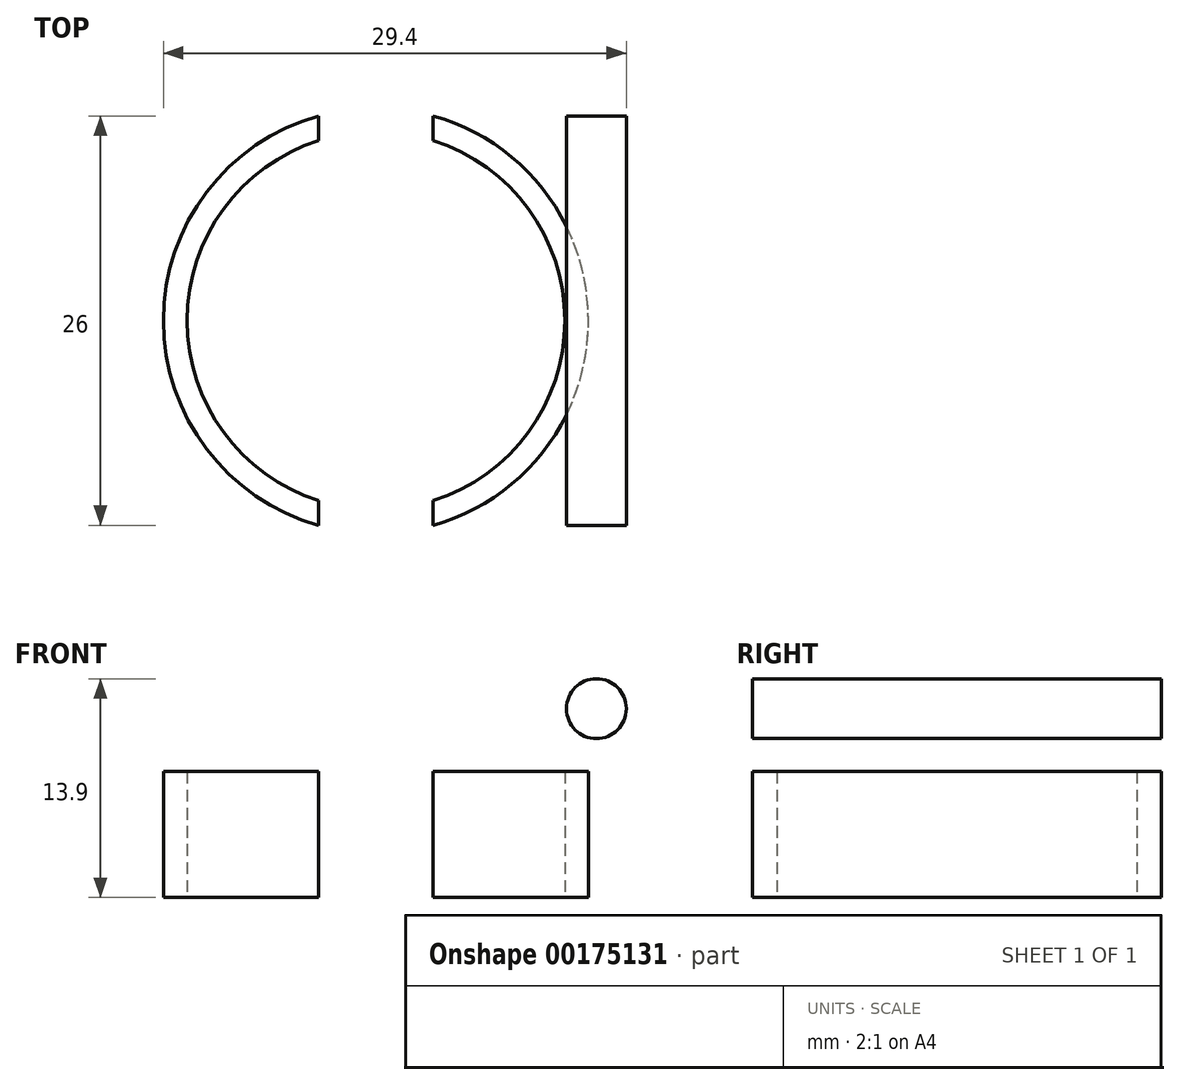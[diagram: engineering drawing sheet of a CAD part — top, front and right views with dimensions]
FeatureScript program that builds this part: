
annotation { "Feature Type Name" : "Feature", "Feature Type Description" : "" }
export const myFeature = defineFeature(function(context is Context, id is Id, definition is map)
    precondition{}
    {
        {
            var Q0;
            Q0=qCreatedBy(makeId("Top.planeOp"),FACE);
            var sketch = newSketch(context, id + "F0", { "sketchPlane" : qUnion([Q0])});
            skCircle(sketch, "E0", {"center": v(0, 0) * mm, "radius": 12 * mm});
            skCircle(sketch, "E1", {"center": v(0, 0) * mm, "radius": 10.25 * mm});
            skCircle(sketch, "E2", {"center": v(0, 0) * mm, "radius": 4.25 * mm});
            skCircle(sketch, "E3", {"center": v(0, 0) * mm, "radius": 2.6 * mm});
            skCircle(sketch, "E4", {"center": v(0, -7) * mm, "radius": 2.6 * mm});
            skCircle(sketch, "E5", {"center": v(0, 0) * mm, "radius": 7 * mm, "construction": true});
            skCircle(sketch, "E6", {"center": v(-7, 0) * mm, "radius": 1.6 * mm});
            skCircle(sketch, "E7", {"center": v(7, 0) * mm, "radius": 1.6 * mm});
            skCircle(sketch, "E8", {"center": v(0, 7) * mm, "radius": 1.6 * mm});
            skCircle(sketch, "E9", {"center": v(4.95, 4.95) * mm, "radius": 1.6 * mm});
            skCircle(sketch, "E10.MirrorC", {"center": v(-4.95, 4.95) * mm, "radius": 1.6 * mm});
            skCircle(sketch, "E11", {"center": v(0, 0) * mm, "radius": 13.5 * mm});
            skLineSegment(sketch, "E12", {"start": v(-3.38, 13.07) * mm, "end": v(-2.98, 11.62) * mm});
            skLineSegment(sketch, "E13", {"start": v(-13, 3.65) * mm, "end": v(-11.53, 3.32) * mm});
            skLineSegment(sketch, "E14.MirrorCS", {"start": v(3.38, 13.07) * mm, "end": v(2.98, 11.62) * mm});
            skLineSegment(sketch, "E15.MirrorCS", {"start": v(13, 3.65) * mm, "end": v(11.53, 3.32) * mm});
            skLineSegment(sketch, "E16.MirrorCS", {"start": v(-13, -3.65) * mm, "end": v(-11.53, -3.32) * mm});
            skLineSegment(sketch, "E17.MirrorCS", {"start": v(-3.38, -13.07) * mm, "end": v(-2.98, -11.62) * mm});
            skLineSegment(sketch, "E18.MirrorCS", {"start": v(3.38, -13.07) * mm, "end": v(2.98, -11.62) * mm});
            skLineSegment(sketch, "E19.MirrorCS", {"start": v(13, -3.65) * mm, "end": v(11.53, -3.32) * mm});
            skLineSegment(sketch, "E20.bottom", {"start": v(16.5, 13) * mm, "end": v(-16.5, 13) * mm});
            skLineSegment(sketch, "E20.top", {"start": v(16.5, -13) * mm, "end": v(-16.5, -13) * mm});
            skLineSegment(sketch, "E20.left", {"start": v(16.5, 13) * mm, "end": v(16.5, -13) * mm});
            skLineSegment(sketch, "E20.right", {"start": v(-16.5, 13) * mm, "end": v(-16.5, -13) * mm});
            skSolve(sketch);
        }
        {
            var Q0;
            Q0=makeQuery(id+"F0.imprint","IMPRINT",FACE,{"disambiguationData":[TD([[makeQuery(id+"F0.imprint","IMPRINT",EDGE,{"derivedFrom":sQuery(id+"F0.wireOp",EDGE,"E2")}),1.0]])]});
            extrude(context, id + "F1", {"entities" : qUnion([Q0]), "depth" : 8 * mm});
        }
        {
            var Q0;
            Q0=makeQuery(id+"F0.imprint","IMPRINT",FACE,{"disambiguationData":[TD([[makeQuery(id+"F0.imprint","IMPRINT",EDGE,{"derivedFrom":sQuery(id+"F0.wireOp",EDGE,"E1")}),1.0]])]});
            extrude(context, id + "F2", {"entities" : qUnion([Q0]), "operationType" : NewBodyOperationType.ADD, "depth" : 8 * mm});
        }
        {
            var Q0;
            Q0=makeQuery(id+"F0.imprint","IMPRINT",FACE,{"disambiguationData":[TD([[makeQuery(id+"F0.imprint","IMPRINT",EDGE,{"derivedFrom":sQuery(id+"F0.wireOp",EDGE,"E0")}),1.0]])]});
            var Q1;
            {var subQ0=sQuery(id+"F0.wireOp",EDGE,"E15.MirrorCS");Q1=makeQuery(id+"F0.imprint","IMPRINT",FACE,{"disambiguationData":[TD([[makeQuery(id+"F0.imprint","IMPRINT",EDGE,{"derivedFrom":subQ0}),-1.0]])]});}
            var Q2;
            {var subQ0=sQuery(id+"F0.wireOp",EDGE,"E12");var subQ1=sQuery(id+"F0.wireOp",EDGE,"E0");var subQ2=makeQuery(id+"F0.imprint","INTERSECT",VERTEX,{"derivedFrom":[subQ1,subQ0]});Q2=makeQuery(id+"F0.imprint","IMPRINT",FACE,{"disambiguationData":[TD([[makeQuery(id+"F0.imprint","IMPRINT",EDGE,{"disambiguationData":[TD([[subQ2,1.0]])],"derivedFrom":subQ1}),-1.0]])]});}
            var Q3;
            {var subQ0=sQuery(id+"F0.wireOp",EDGE,"E20.left");Q3=makeQuery(id+"F0.imprint","IMPRINT",FACE,{"disambiguationData":[TD([[makeQuery(id+"F0.imprint","IMPRINT",EDGE,{"derivedFrom":subQ0}),-1.0]])]});}
            var Q4;
            {var subQ0=sQuery(id+"F0.wireOp",EDGE,"E15.MirrorCS");Q4=makeQuery(id+"F0.imprint","IMPRINT",FACE,{"disambiguationData":[TD([[makeQuery(id+"F0.imprint","IMPRINT",EDGE,{"derivedFrom":subQ0}),1.0]])]});}
            var Q5;
            {var subQ0=sQuery(id+"F0.wireOp",EDGE,"E19.MirrorCS");Q5=makeQuery(id+"F0.imprint","IMPRINT",FACE,{"disambiguationData":[TD([[makeQuery(id+"F0.imprint","IMPRINT",EDGE,{"derivedFrom":subQ0}),1.0]])]});}
            var Q6;
            {var subQ0=sQuery(id+"F0.wireOp",EDGE,"E17.MirrorCS");var subQ1=sQuery(id+"F0.wireOp",EDGE,"E0");var subQ2=makeQuery(id+"F0.imprint","INTERSECT",VERTEX,{"derivedFrom":[subQ1,subQ0]});Q6=makeQuery(id+"F0.imprint","IMPRINT",FACE,{"disambiguationData":[TD([[makeQuery(id+"F0.imprint","IMPRINT",EDGE,{"disambiguationData":[TD([[subQ2,-1.0]])],"derivedFrom":subQ1}),-1.0]])]});}
            var Q7;
            {var subQ0=sQuery(id+"F0.wireOp",EDGE,"E16.MirrorCS");Q7=makeQuery(id+"F0.imprint","IMPRINT",FACE,{"disambiguationData":[TD([[makeQuery(id+"F0.imprint","IMPRINT",EDGE,{"derivedFrom":subQ0}),-1.0]])]});}
            var Q8;
            {var subQ0=sQuery(id+"F0.wireOp",EDGE,"E20.right");Q8=makeQuery(id+"F0.imprint","IMPRINT",FACE,{"disambiguationData":[TD([[makeQuery(id+"F0.imprint","IMPRINT",EDGE,{"derivedFrom":subQ0}),1.0]])]});}
            var Q9;
            {var subQ0=sQuery(id+"F0.wireOp",EDGE,"E13");Q9=makeQuery(id+"F0.imprint","IMPRINT",FACE,{"disambiguationData":[TD([[makeQuery(id+"F0.imprint","IMPRINT",EDGE,{"derivedFrom":subQ0}),-1.0]])]});}
            var Q10;
            {var subQ0=sQuery(id+"F0.wireOp",EDGE,"E13");Q10=makeQuery(id+"F0.imprint","IMPRINT",FACE,{"disambiguationData":[TD([[makeQuery(id+"F0.imprint","IMPRINT",EDGE,{"derivedFrom":subQ0}),1.0]])]});}
            extrude(context, id + "F3", {"entities" : qUnion([Q0, Q1, Q2, Q3, Q4, Q5, Q6, Q7, Q8, Q9, Q10]), "operationType" : NewBodyOperationType.ADD, "depth" : 8 * mm});
        }
        {
            var Q0;
            {var subQ0=sQuery(id+"F0.wireOp",EDGE,"E16.MirrorCS");Q0=makeQuery(id+"F0.imprint","IMPRINT",FACE,{"disambiguationData":[TD([[makeQuery(id+"F0.imprint","IMPRINT",EDGE,{"derivedFrom":subQ0}),-1.0]])]});}
            var Q1;
            {var subQ0=sQuery(id+"F0.wireOp",EDGE,"E19.MirrorCS");Q1=makeQuery(id+"F0.imprint","IMPRINT",FACE,{"disambiguationData":[TD([[makeQuery(id+"F0.imprint","IMPRINT",EDGE,{"derivedFrom":subQ0}),1.0]])]});}
            var Q2;
            {var subQ0=sQuery(id+"F0.wireOp",EDGE,"E15.MirrorCS");Q2=makeQuery(id+"F0.imprint","IMPRINT",FACE,{"disambiguationData":[TD([[makeQuery(id+"F0.imprint","IMPRINT",EDGE,{"derivedFrom":subQ0}),-1.0]])]});}
            var Q3;
            {var subQ0=sQuery(id+"F0.wireOp",EDGE,"E13");Q3=makeQuery(id+"F0.imprint","IMPRINT",FACE,{"disambiguationData":[TD([[makeQuery(id+"F0.imprint","IMPRINT",EDGE,{"derivedFrom":subQ0}),1.0]])]});}
            var Q4;
            {var subQ0=sQuery(id+"F0.wireOp",EDGE,"E17.MirrorCS");var subQ1=sQuery(id+"F0.wireOp",EDGE,"E0");var subQ2=makeQuery(id+"F0.imprint","INTERSECT",VERTEX,{"derivedFrom":[subQ1,subQ0]});Q4=makeQuery(id+"F0.imprint","IMPRINT",FACE,{"disambiguationData":[TD([[makeQuery(id+"F0.imprint","IMPRINT",EDGE,{"disambiguationData":[TD([[subQ2,-1.0]])],"derivedFrom":subQ1}),-1.0]])]});}
            var Q5;
            {var subQ0=sQuery(id+"F0.wireOp",EDGE,"E13");Q5=makeQuery(id+"F0.imprint","IMPRINT",FACE,{"disambiguationData":[TD([[makeQuery(id+"F0.imprint","IMPRINT",EDGE,{"derivedFrom":subQ0}),-1.0]])]});}
            var Q6;
            {var subQ0=sQuery(id+"F0.wireOp",EDGE,"E15.MirrorCS");Q6=makeQuery(id+"F0.imprint","IMPRINT",FACE,{"disambiguationData":[TD([[makeQuery(id+"F0.imprint","IMPRINT",EDGE,{"derivedFrom":subQ0}),1.0]])]});}
            var Q7;
            {var subQ0=sQuery(id+"F0.wireOp",EDGE,"E12");var subQ1=sQuery(id+"F0.wireOp",EDGE,"E0");var subQ2=makeQuery(id+"F0.imprint","INTERSECT",VERTEX,{"derivedFrom":[subQ1,subQ0]});Q7=makeQuery(id+"F0.imprint","IMPRINT",FACE,{"disambiguationData":[TD([[makeQuery(id+"F0.imprint","IMPRINT",EDGE,{"disambiguationData":[TD([[subQ2,1.0]])],"derivedFrom":subQ1}),-1.0]])]});}
            extrude(context, id + "F4", {"entities" : qUnion([Q0, Q1, Q2, Q3, Q4, Q5, Q6, Q7]), "operationType" : NewBodyOperationType.ADD, "endBound" : BoundingType.SYMMETRIC, "depth" : 16 * mm});
        }
        {
            var Q0;
            {var subQ0=sQuery(id+"F0.wireOp",EDGE,"E20.top");Q0=makeQuery(id+"F4.boolean.opBoolean","MERGE",FACE,{"derivedFrom":[makeQuery(id+"F3.opExtrude","SWEPT_FACE",FACE,{"disambiguationData":[OSD([subQ0])]}),makeQuery(id+"F4.opExtrude","SWEPT_FACE",FACE,{"disambiguationData":[OSD([subQ0])]})]});}
            var sketch = newSketch(context, id + "F5", { "sketchPlane" : qUnion([Q0])});
            skCircle(sketch, "E21", {"center": v(-14, 4) * mm, "radius": 1.9 * mm});
            skCircle(sketch, "E22.MirrorC", {"center": v(14, 4) * mm, "radius": 1.9 * mm});
            skSolve(sketch);
        }
        {
            var Q0;
            Q0=makeQuery(id+"F5.imprint","IMPRINT",FACE,{"disambiguationData":[TD([[makeQuery(id+"F5.imprint","IMPRINT",EDGE,{"derivedFrom":sQuery(id+"F5.wireOp",EDGE,"E21")}),1.0]])]});
            var Q1;
            Q1=makeQuery(id+"F5.imprint","IMPRINT",FACE,{"disambiguationData":[TD([[makeQuery(id+"F5.imprint","IMPRINT",EDGE,{"derivedFrom":sQuery(id+"F5.wireOp",EDGE,"E22.MirrorC")}),-1.0]])]});
            extrude(context, id + "F6", {"entities" : qUnion([Q0, Q1]), "operationType" : NewBodyOperationType.REMOVE, "oppositeDirection" : true, "depth" : 27 * mm});
        }
    });
